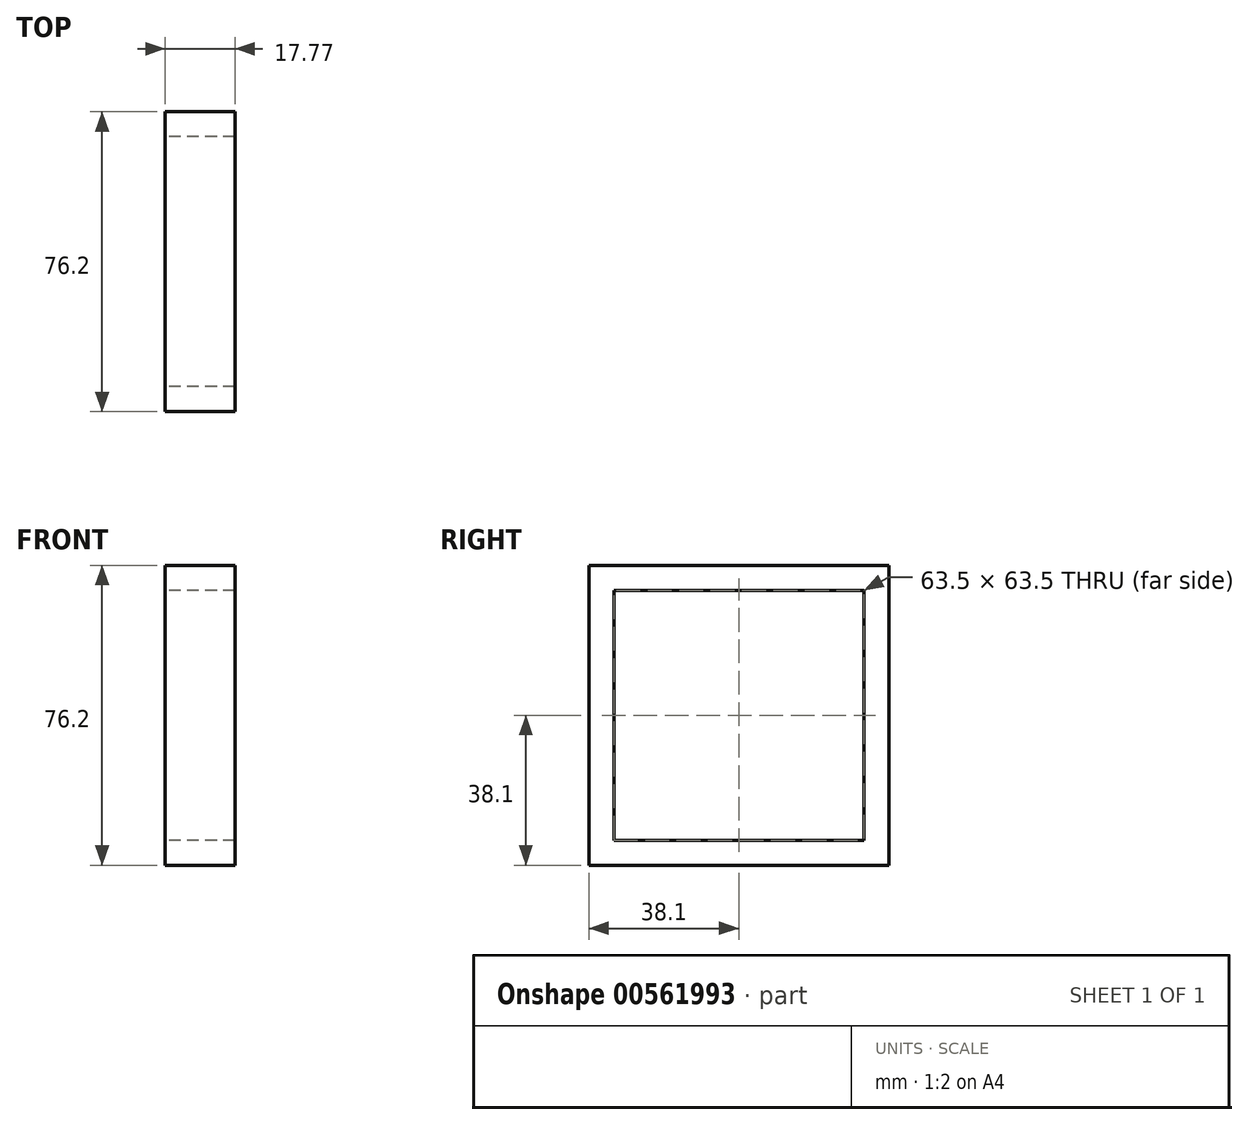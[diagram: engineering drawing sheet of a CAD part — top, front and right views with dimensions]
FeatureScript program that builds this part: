
annotation { "Feature Type Name" : "Feature", "Feature Type Description" : "" }
export const myFeature = defineFeature(function(context is Context, id is Id, definition is map)
    precondition{}
    {
        {
            assignVariable(context, id + "F0", {"name" : "length", "anyValue" : 17.77});
        }
        {
            var Q0;
            Q0=qCreatedBy(makeId("Right.planeOp"),FACE);
            var sketch = newSketch(context, id + "F1", { "sketchPlane" : qUnion([Q0])});
            skLineSegment(sketch, "E0.bottom", {"start": v(38.1, -38.1) * mm, "end": v(-38.1, -38.1) * mm});
            skLineSegment(sketch, "E0.top", {"start": v(38.1, 38.1) * mm, "end": v(-38.1, 38.1) * mm});
            skLineSegment(sketch, "E0.left", {"start": v(38.1, -38.1) * mm, "end": v(38.1, 38.1) * mm});
            skLineSegment(sketch, "E0.right", {"start": v(-38.1, -38.1) * mm, "end": v(-38.1, 38.1) * mm});
            skPoint(sketch, "E0.middle", {"position": v(0, 0) * mm});
            skLineSegment(sketch, "E1", {"start": v(0, 0) * mm, "end": v(-38.1, 38.1) * mm, "construction": true});
            skLineSegment(sketch, "E2.bottom", {"start": v(31.75, -31.75) * mm, "end": v(-31.75, -31.75) * mm});
            skLineSegment(sketch, "E2.top", {"start": v(31.75, 31.75) * mm, "end": v(-31.75, 31.75) * mm});
            skLineSegment(sketch, "E2.left", {"start": v(31.75, -31.75) * mm, "end": v(31.75, 31.75) * mm});
            skLineSegment(sketch, "E2.right", {"start": v(-31.75, -31.75) * mm, "end": v(-31.75, 31.75) * mm});
            skSolve(sketch);
        }
        {
            var Q0;
            Q0=makeQuery(id+"F1.imprint","IMPRINT",FACE,{"disambiguationData":[TD([[makeQuery(id+"F1.imprint","IMPRINT",EDGE,{"derivedFrom":sQuery(id+"F1.wireOp",EDGE,"E0.bottom")}),-1.0]])]});
            extrude(context, id + "F2", {"entities" : qUnion([Q0]), "depth" : (getVariable(context, 'length')) * mm, "offsetDistance" : 25.4 * mm});
        }
        {
            var Q0;
            Q0=makeQuery(id+"F2.opExtrude","SWEPT_FACE",FACE,{"disambiguationData":[OSD([sQuery(id+"F1.wireOp",EDGE,"E0.right")])]});
            var sketch = newSketch(context, id + "F3", { "sketchPlane" : qUnion([Q0])});
            skLineSegment(sketch, "E3", {"start": v(0, 0) * mm, "end": v(451.33, 0) * mm, "construction": true});
            skCircle(sketch, "E4", {"center": v(152.4, 0) * mm, "radius": 7.14 * mm});
            skCircle(sketch, "E5", {"center": v(127.66, 0) * mm, "radius": 7.14 * mm});
            skSolve(sketch);
        }
        {
            var Q0;
            Q0 = qSketchRegion(id + "F3", true);
            extrude(context, id + "F4", {"entities" : qUnion([Q0]), "operationType" : NewBodyOperationType.REMOVE, "endBound" : BoundingType.THROUGH_ALL, "oppositeDirection" : true, "depth" : 25.4 * mm, "offsetDistance" : 25.4 * mm});
        }
    });
